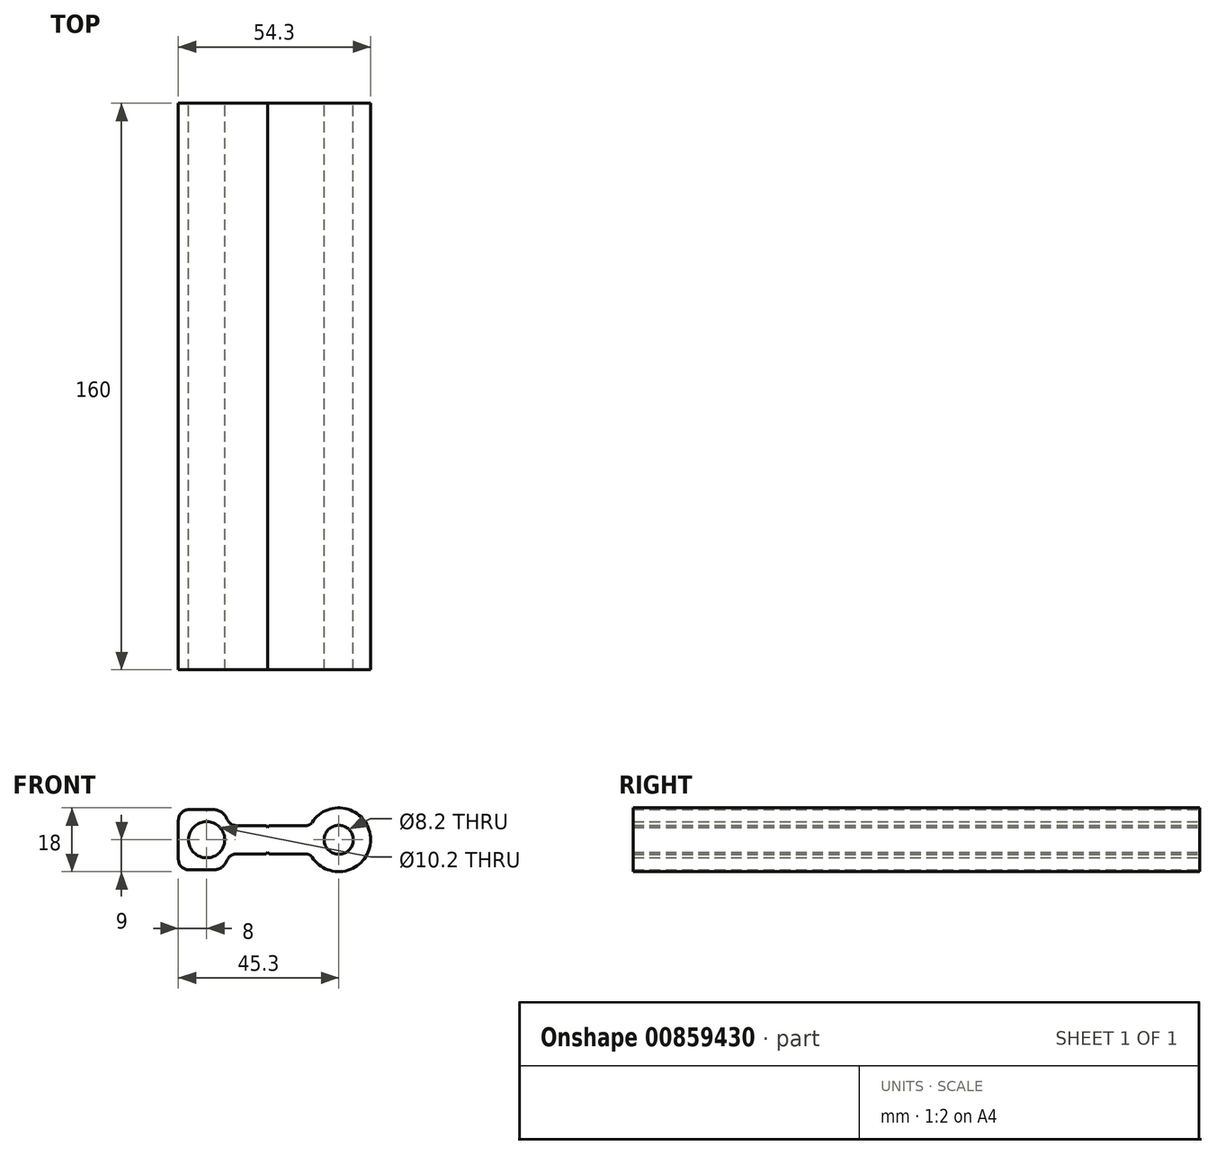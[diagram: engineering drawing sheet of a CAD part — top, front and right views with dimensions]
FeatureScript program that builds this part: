
annotation { "Feature Type Name" : "Feature", "Feature Type Description" : "" }
export const myFeature = defineFeature(function(context is Context, id is Id, definition is map)
    precondition{}
    {
        {
            var Q0;
            Q0=qCreatedBy(makeId("Front.planeOp"),FACE);
            var sketch = newSketch(context, id + "F0", { "sketchPlane" : qUnion([Q0])});
            skArc(sketch, "E0", {"start": v(-7.54, -4.9) * mm, "mid": v(9, 0) * mm, "end": v(-7.54, 4.9) * mm});
            skCircle(sketch, "E1", {"center": v(0, 0) * mm, "radius": 4.1 * mm});
            skLineSegment(sketch, "E2", {"start": v(0, 0) * mm, "end": v(0, 0) * mm});
            skLineSegment(sketch, "E3", {"start": v(-18.65, 0) * mm, "end": v(-18.65, 4) * mm, "construction": true});
            skLineSegment(sketch, "E4", {"start": v(-18.65, 0) * mm, "end": v(-18.65, -4) * mm, "construction": true});
            skLineSegment(sketch, "E5", {"start": v(9, 0) * mm, "end": v(-18.65, 0) * mm, "construction": true});
            skLineSegment(sketch, "E6", {"start": v(-45.3, 5.5) * mm, "end": v(-45.3, -5.5) * mm});
            skLineSegment(sketch, "E7", {"start": v(-22.85, 0) * mm, "end": v(-22.85, 8.5) * mm, "construction": true});
            skLineSegment(sketch, "E8", {"start": v(-22.85, 0) * mm, "end": v(-22.85, -8.5) * mm, "construction": true});
            skLineSegment(sketch, "E9", {"start": v(-42.3, 8.5) * mm, "end": v(-35.36, 8.5) * mm});
            skLineSegment(sketch, "E10", {"start": v(-9.22, 4) * mm, "end": v(-19.48, 4) * mm});
            skLineSegment(sketch, "E11", {"start": v(-9.22, -4) * mm, "end": v(-19.48, -4) * mm});
            skLineSegment(sketch, "E12", {"start": v(-45.3, 9.4) * mm, "end": v(-34.97, 9.4) * mm, "construction": true});
            skLineSegment(sketch, "E13", {"start": v(-34.97, 9.4) * mm, "end": v(-34.97, -9.97) * mm, "construction": true});
            skLineSegment(sketch, "E14", {"start": v(-45.3, 4) * mm, "end": v(-28.82, 4) * mm, "construction": true});
            skLineSegment(sketch, "E15", {"start": v(-45.3, 6.62) * mm, "end": v(-31.36, 6.62) * mm, "construction": true});
            skPoint(sketch, "E16.newPointB", {"position": v(-31.36, 10.57) * mm});
            skArc(sketch, "E16.filletArc", {"start": v(-31.62, 5.93) * mm, "mid": v(-33.1, 7.8) * mm, "end": v(-35.36, 8.5) * mm});
            skPoint(sketch, "E17.newPointB", {"position": v(-28.9, 4) * mm});
            skArc(sketch, "E17.filletArc", {"start": v(-31.62, 5.93) * mm, "mid": v(-30.52, 4.53) * mm, "end": v(-28.82, 4) * mm});
            skPoint(sketch, "E18.newPointA", {"position": v(-31.62, -8.5) * mm});
            skPoint(sketch, "E19.newPointA", {"position": v(-45.3, 8.5) * mm});
            skPoint(sketch, "E19.newPointB", {"position": v(-45.3, 10.52) * mm});
            skArc(sketch, "E19.filletArc", {"start": v(-42.3, 8.5) * mm, "mid": v(-44.42, 7.62) * mm, "end": v(-45.3, 5.5) * mm});
            skPoint(sketch, "E20.newPointB", {"position": v(-45.3, -8.5) * mm});
            skArc(sketch, "E20.filletArc", {"start": v(-45.3, -5.5) * mm, "mid": v(-44.42, -7.62) * mm, "end": v(-42.3, -8.5) * mm});
            skPoint(sketch, "E21.visualSharp", {"position": v(-8.06, -4) * mm});
            skArc(sketch, "E21.filletArc", {"start": v(-7.54, -4.9) * mm, "mid": v(-8.27, -4.24) * mm, "end": v(-9.22, -4) * mm});
            skPoint(sketch, "E22.visualSharp", {"position": v(-8.06, 4) * mm});
            skArc(sketch, "E22.filletArc", {"start": v(-9.22, 4) * mm, "mid": v(-8.27, 4.24) * mm, "end": v(-7.54, 4.9) * mm});
            skLineSegment(sketch, "E23", {"start": v(-45.3, 1.35) * mm, "end": v(-20.1, 1.35) * mm, "construction": true});
            skLineSegment(sketch, "E24", {"start": v(-19.69, 3.91) * mm, "end": v(-20.1, 3.5) * mm});
            skLineSegment(sketch, "E25", {"start": v(-20.51, 3.91) * mm, "end": v(-20.1, 3.5) * mm});
            skLineSegment(sketch, "E26.trimOffspring", {"start": v(-20.72, 4) * mm, "end": v(-28.82, 4) * mm});
            skPoint(sketch, "E27.visualSharp", {"position": v(-19.6, 4) * mm});
            skArc(sketch, "E27.filletArc", {"start": v(-19.48, 4) * mm, "mid": v(-19.6, 3.98) * mm, "end": v(-19.69, 3.91) * mm});
            skPoint(sketch, "E28.visualSharp", {"position": v(-20.6, 4) * mm});
            skArc(sketch, "E28.filletArc", {"start": v(-20.51, 3.91) * mm, "mid": v(-20.6, 3.98) * mm, "end": v(-20.72, 4) * mm});
            skCircle(sketch, "E29", {"center": v(-37.3, 0) * mm, "radius": 5.1 * mm});
            skPoint(sketch, "E30.end.orphan", {"position": v(-20.6, 4.2) * mm});
            skPoint(sketch, "E31.end.orphan", {"position": v(-19.6, 4.2) * mm});
            skLineSegment(sketch, "E32", {"start": v(-19.69, -3.91) * mm, "end": v(-20.1, -3.5) * mm});
            skLineSegment(sketch, "E33", {"start": v(-20.51, -3.91) * mm, "end": v(-20.1, -3.5) * mm});
            skPoint(sketch, "E34.orphan", {"position": v(-19.59, -3.5) * mm});
            skPoint(sketch, "E35.end.orphan", {"position": v(-19.6, -4.27) * mm});
            skPoint(sketch, "E36.end.orphan", {"position": v(-20.6, -4.27) * mm});
            skPoint(sketch, "E37.visualSharp", {"position": v(-19.6, -4) * mm});
            skArc(sketch, "E37.filletArc", {"start": v(-19.69, -3.91) * mm, "mid": v(-19.6, -3.98) * mm, "end": v(-19.48, -4) * mm});
            skPoint(sketch, "E38.visualSharp", {"position": v(-20.6, -4) * mm});
            skArc(sketch, "E38.filletArc", {"start": v(-20.72, -4) * mm, "mid": v(-20.6, -3.98) * mm, "end": v(-20.51, -3.91) * mm});
            skArc(sketch, "E39.MirrorCS", {"start": v(-31.62, -5.93) * mm, "mid": v(-30.52, -4.53) * mm, "end": v(-28.82, -4) * mm});
            skArc(sketch, "E40.MirrorCS", {"start": v(-31.62, -5.93) * mm, "mid": v(-33.1, -7.8) * mm, "end": v(-35.36, -8.5) * mm});
            skLineSegment(sketch, "E41", {"start": v(-42.3, -8.5) * mm, "end": v(-35.36, -8.5) * mm});
            skLineSegment(sketch, "E42", {"start": v(-28.82, -4) * mm, "end": v(-20.72, -4) * mm});
            skSolve(sketch);
        }
        {
            var Q0;
            Q0=makeQuery(id+"F0.imprint","IMPRINT",FACE,{"disambiguationData":[TD([[makeQuery(id+"F0.imprint","IMPRINT",EDGE,{"derivedFrom":sQuery(id+"F0.wireOp",EDGE,"E0")}),1.0]])]});
            extrude(context, id + "F1", {"entities" : qUnion([Q0]), "depth" : 160 * mm, "offsetDistance" : 25 * mm});
        }
    });
